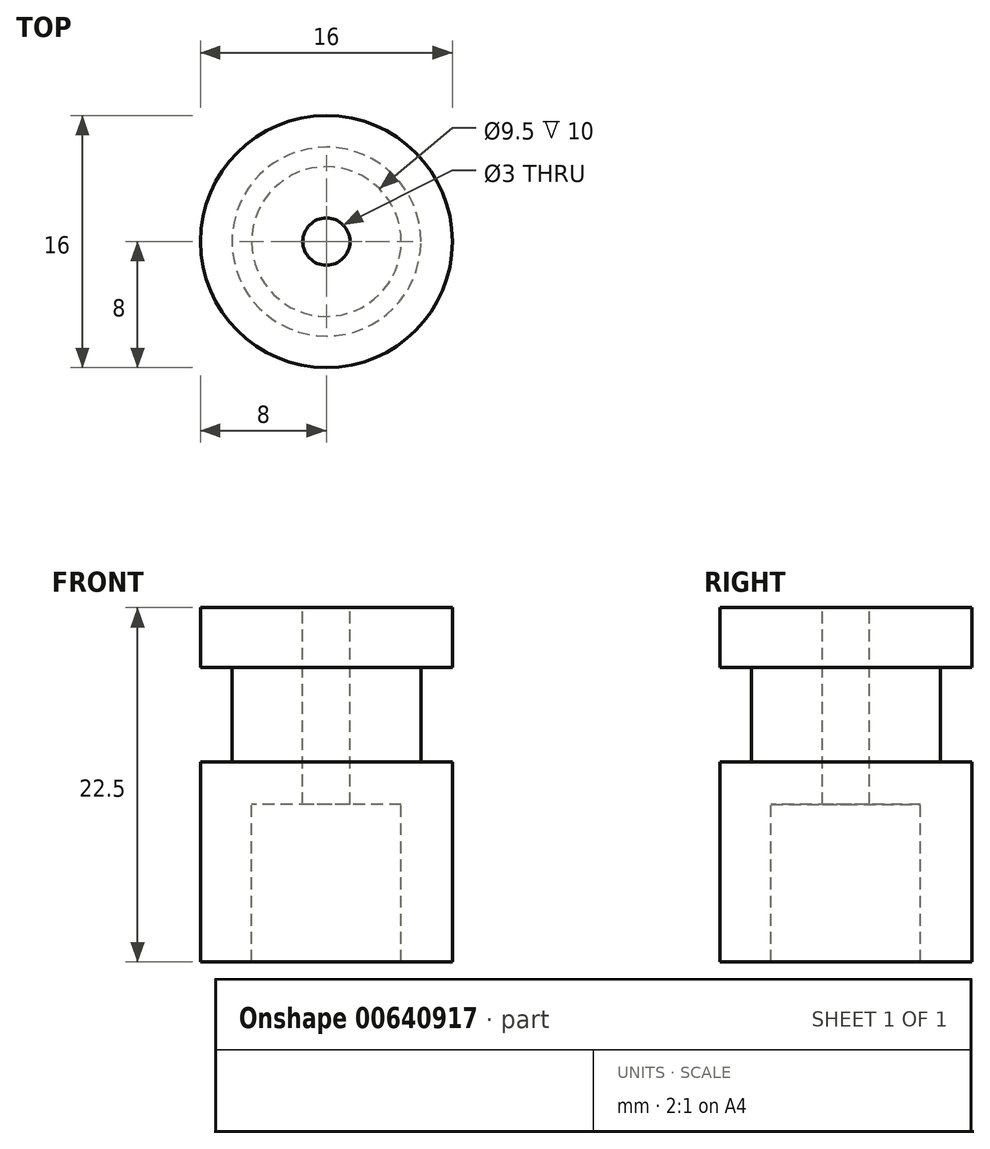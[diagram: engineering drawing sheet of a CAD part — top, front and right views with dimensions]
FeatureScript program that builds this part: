
annotation { "Feature Type Name" : "Feature", "Feature Type Description" : "" }
export const myFeature = defineFeature(function(context is Context, id is Id, definition is map)
    precondition{}
    {
        {
            var Q0;
            Q0=qCreatedBy(makeId("Front.planeOp"),FACE);
            var sketch = newSketch(context, id + "F0", { "sketchPlane" : qUnion([Q0])});
            skLineSegment(sketch, "E0", {"start": v(-4.75, 0) * mm, "end": v(-8, 0) * mm});
            skLineSegment(sketch, "E1", {"start": v(-8, 0) * mm, "end": v(-8, 12.7) * mm});
            skLineSegment(sketch, "E2", {"start": v(-8, 12.7) * mm, "end": v(-6, 12.7) * mm});
            skLineSegment(sketch, "E3", {"start": v(-6, 12.7) * mm, "end": v(-6, 18.7) * mm});
            skLineSegment(sketch, "E4", {"start": v(-6, 18.7) * mm, "end": v(-8, 18.7) * mm});
            skLineSegment(sketch, "E5", {"start": v(-8, 18.7) * mm, "end": v(-8, 22.5) * mm});
            skLineSegment(sketch, "E6", {"start": v(-8, 22.5) * mm, "end": v(-1.5, 22.5) * mm});
            skLineSegment(sketch, "E7", {"start": v(0, 22.5) * mm, "end": v(0, 0) * mm});
            skLineSegment(sketch, "E8", {"start": v(0, 18.05) * mm, "end": v(0, -5.56) * mm, "construction": true});
            skLineSegment(sketch, "E9", {"start": v(-1.5, 22.5) * mm, "end": v(-1.5, 10) * mm});
            skLineSegment(sketch, "E10", {"start": v(-1.5, 10) * mm, "end": v(-4.75, 10) * mm});
            skLineSegment(sketch, "E11", {"start": v(-4.75, 10) * mm, "end": v(-4.75, 0) * mm});
            skSolve(sketch);
        }
        {
            var Q0;
            Q0 = qSketchRegion(id + "F0", true);
            var Q1;
            Q1=sQuery(id+"F0.wireOp",EDGE,"E7");
            revolve(context, id + "F1", {"entities" : qUnion([Q0]), "axis" : qUnion([Q1]), "revolveType" : RevolveType.FULL});
        }
    });
